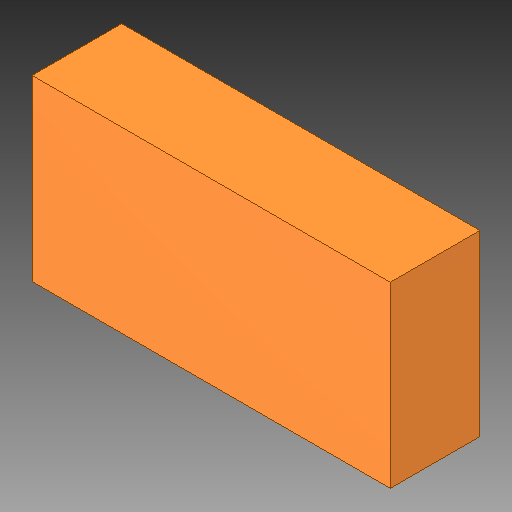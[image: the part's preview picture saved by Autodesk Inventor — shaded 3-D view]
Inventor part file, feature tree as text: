
AUTODESK INVENTOR PART (.ipt)
format: ipt  version: 2019 (Build 230136000, 136)  size: 88,064 bytes
history: native  units: in
note: dims shown in document units (in); Inventor stores cm internally (conversion verified against a paired STEP export)
features: extrude x1, other x1
ambient origin geometry x8: Origin, YZ Plane, XZ Plane, XY Plane, X Axis, Y Axis, Z Axis, Center Point
bodies: Solid1 (feature_tree)
feature tree (2):
  extrude  "Extrusion1"  Depth=0.0394in TaperAngle=0.0deg
  other  "M0805, 10K_16"
